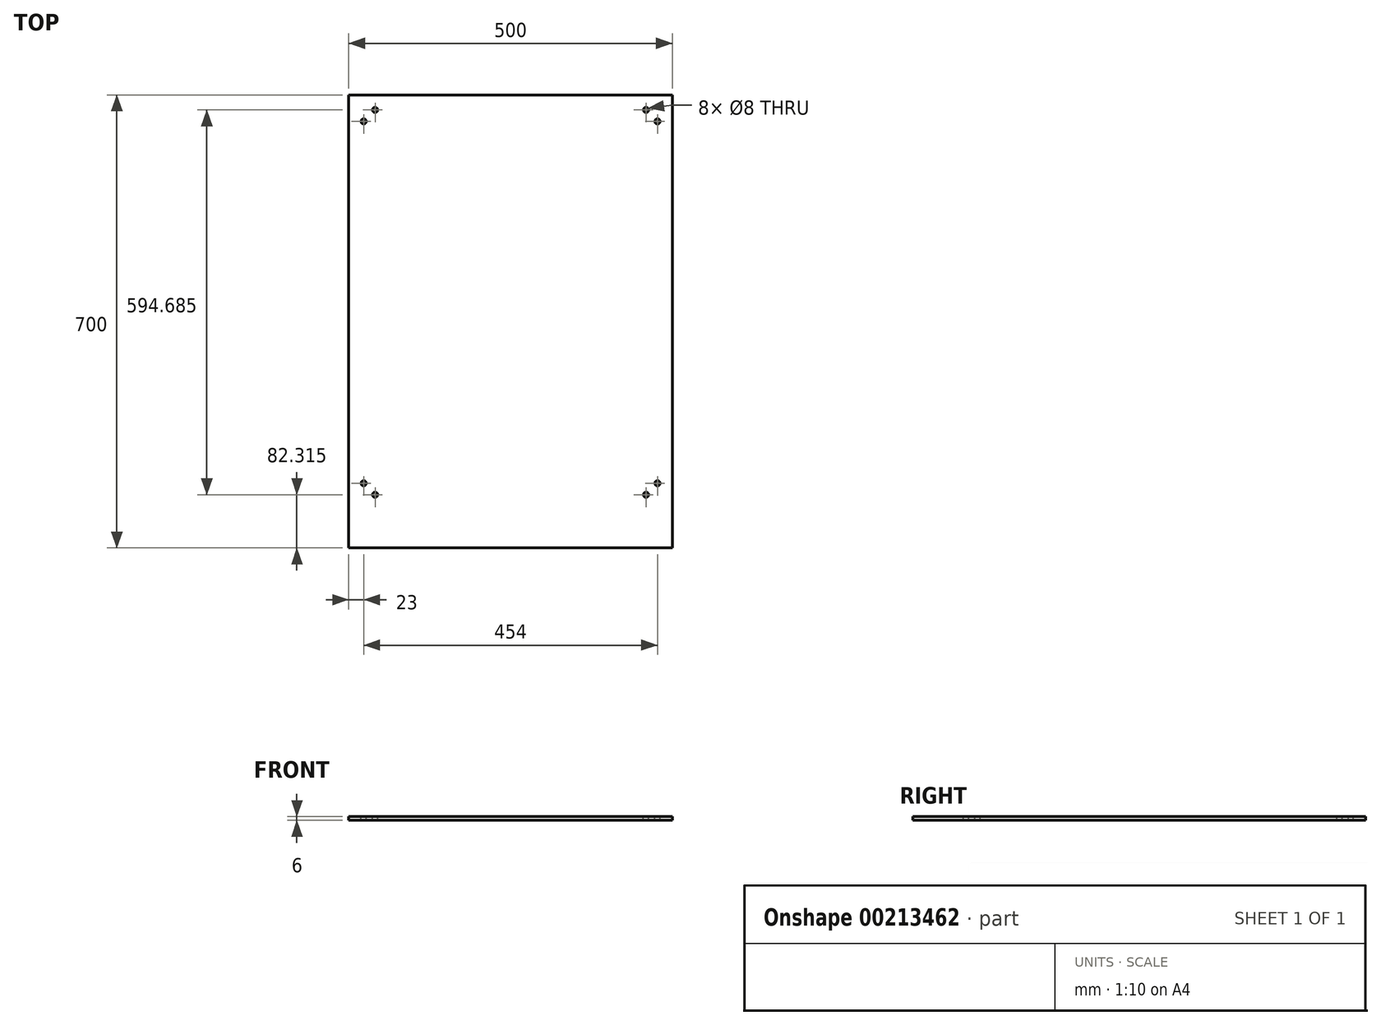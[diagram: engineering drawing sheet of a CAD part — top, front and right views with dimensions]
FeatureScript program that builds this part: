
annotation { "Feature Type Name" : "Feature", "Feature Type Description" : "" }
export const myFeature = defineFeature(function(context is Context, id is Id, definition is map)
    precondition{}
    {
        {
            var Q0;
            Q0=qCreatedBy(makeId("Right.planeOp"),FACE);
            var sketch = newSketch(context, id + "F0", { "sketchPlane" : qUnion([Q0])});
            skLineSegment(sketch, "E0.bottom", {"start": v(0, 0) * mm, "end": v(700, 0) * mm});
            skLineSegment(sketch, "E0.top", {"start": v(0, -6) * mm, "end": v(700, -6) * mm});
            skLineSegment(sketch, "E0.right", {"start": v(700, 0) * mm, "end": v(700, -6) * mm});
            skLineSegment(sketch, "E1", {"start": v(0, 0) * mm, "end": v(-98.48, 17.36) * mm});
            skLineSegment(sketch, "E2", {"start": v(-98.48, 17.36) * mm, "end": v(-99.52, 11.46) * mm});
            skLineSegment(sketch, "E3", {"start": v(-99.52, 11.46) * mm, "end": v(0, -6) * mm});
            skSolve(sketch);
        }
        {
            var Q0;
            Q0=makeQuery(id+"F0.imprint","IMPRINT",FACE,{"disambiguationData":[TD([[makeQuery(id+"F0.imprint","IMPRINT",EDGE,{"derivedFrom":sQuery(id+"F0.wireOp",EDGE,"E0.bottom")}),-1.0]])]});
            extrude(context, id + "F1", {"entities" : qUnion([Q0]), "depth" : 500 * mm});
        }
        {
            var Q0;
            Q0=makeQuery(id+"F1.opExtrude","SWEPT_FACE",FACE,{"disambiguationData":[OSD([sQuery(id+"F0.wireOp",EDGE,"E1")])]});
            var sketch = newSketch(context, id + "F2", { "sketchPlane" : qUnion([Q0])});
            skLineSegment(sketch, "E4", {"start": v(50, -100) * mm, "end": v(450, -100) * mm});
            skPoint(sketch, "E5.visualSharp", {"position": v(0, -100) * mm});
            skArc(sketch, "E5.filletArc", {"start": v(0, -50) * mm, "mid": v(14.64, -85.36) * mm, "end": v(50, -100) * mm});
            skPoint(sketch, "E6.visualSharp", {"position": v(500, -100) * mm});
            skArc(sketch, "E6.filletArc", {"start": v(450, -100) * mm, "mid": v(485.36, -85.36) * mm, "end": v(500, -50) * mm});
            skLineSegment(sketch, "E7.left", {"start": v(0, -50) * mm, "end": v(0, -50) * mm});
            skLineSegment(sketch, "E8", {"start": v(0, -50) * mm, "end": v(-35.02, -50) * mm});
            skLineSegment(sketch, "E9", {"start": v(-35.02, -50) * mm, "end": v(-35.02, -125.84) * mm});
            skLineSegment(sketch, "E10", {"start": v(-35.02, -125.84) * mm, "end": v(549.5, -125.84) * mm});
            skLineSegment(sketch, "E11", {"start": v(549.5, -125.84) * mm, "end": v(549.5, -50) * mm});
            skLineSegment(sketch, "E12", {"start": v(549.5, -50) * mm, "end": v(500, -50) * mm});
            skSolve(sketch);
        }
        {
            var Q0;
            {var subQ0=sQuery(id+"F2.wireOp",EDGE,"E5.filletArc");Q0=makeQuery(id+"F2.imprint","IMPRINT",FACE,{"disambiguationData":[TD([[makeQuery(id+"F2.imprint","IMPRINT",EDGE,{"derivedFrom":subQ0}),-1.0]])]});}
            var Q1;
            {var subQ0=sQuery(id+"F2.wireOp",EDGE,"E6.filletArc");Q1=makeQuery(id+"F2.imprint","IMPRINT",FACE,{"disambiguationData":[TD([[makeQuery(id+"F2.imprint","IMPRINT",EDGE,{"derivedFrom":subQ0}),-1.0]])]});}
            extrude(context, id + "F3", {"entities" : qUnion([Q0, Q1]), "operationType" : NewBodyOperationType.REMOVE, "endBound" : BoundingType.THROUGH_ALL, "oppositeDirection" : true, "depth" : 25 * mm});
        }
        {
            var Q0;
            Q0=makeQuery(id+"F1.opExtrude","SWEPT_FACE",FACE,{"disambiguationData":[OSD([sQuery(id+"F0.wireOp",EDGE,"E0.bottom")])]});
            var sketch = newSketch(context, id + "F4", { "sketchPlane" : qUnion([Q0])});
            skCircle(sketch, "E13", {"center": v(23, 100) * mm, "radius": 4 * mm});
            skLineSegment(sketch, "E14", {"start": v(23, 100) * mm, "end": v(40.68, 82.32) * mm, "construction": true});
            skCircle(sketch, "E15", {"center": v(40.68, 82.32) * mm, "radius": 4 * mm});
            skLineSegment(sketch, "E16", {"start": v(250, 700) * mm, "end": v(250, 0) * mm, "construction": true});
            skCircle(sketch, "E17", {"center": v(23, 659.32) * mm, "radius": 4 * mm});
            skLineSegment(sketch, "E18", {"start": v(23, 659.32) * mm, "end": v(40.68, 677) * mm, "construction": true});
            skCircle(sketch, "E19", {"center": v(40.68, 677) * mm, "radius": 4 * mm});
            skCircle(sketch, "E20.MirrorC", {"center": v(459.32, 677) * mm, "radius": 4 * mm});
            skCircle(sketch, "E21.MirrorC", {"center": v(477, 659.32) * mm, "radius": 4 * mm});
            skCircle(sketch, "E22.MirrorC", {"center": v(477, 100) * mm, "radius": 4 * mm});
            skCircle(sketch, "E23.MirrorC", {"center": v(459.32, 82.32) * mm, "radius": 4 * mm});
            skSolve(sketch);
        }
        {
            var Q0;
            Q0=qSketchRegion(id+"F4",true);
            extrude(context, id + "F5", {"entities" : qUnion([Q0]), "operationType" : NewBodyOperationType.REMOVE, "endBound" : BoundingType.THROUGH_ALL, "oppositeDirection" : true, "depth" : 25 * mm});
        }
        {
            var Q0;
            Q0=makeQuery(id+"F1.opExtrude","SWEPT_FACE",FACE,{"disambiguationData":[OSD([sQuery(id+"F0.wireOp",EDGE,"E0.top")])]});
            var sketch = newSketch(context, id + "F6", { "sketchPlane" : qUnion([Q0])});
            skLineSegment(sketch, "E24.bottom", {"start": v(0, 0) * mm, "end": v(500, 0) * mm});
            skLineSegment(sketch, "E24.top", {"start": v(0, 122.32) * mm, "end": v(500, 122.32) * mm});
            skLineSegment(sketch, "E24.left", {"start": v(0, 0) * mm, "end": v(0, 122.32) * mm});
            skLineSegment(sketch, "E24.right", {"start": v(500, 0) * mm, "end": v(500, 122.32) * mm});
            skSolve(sketch);
        }
        {
            var Q0;
            Q0=makeQuery(id+"F6.imprint","IMPRINT",FACE,{"disambiguationData":[TD([[makeQuery(id+"F6.imprint","IMPRINT",EDGE,{"derivedFrom":sQuery(id+"F6.wireOp",EDGE,"E24.bottom")}),-1.0]])]});
            extrude(context, id + "F7", {"entities" : qUnion([Q0]), "operationType" : NewBodyOperationType.REMOVE, "endBound" : BoundingType.THROUGH_ALL, "oppositeDirection" : true, "depth" : 25 * mm});
        }
    });
